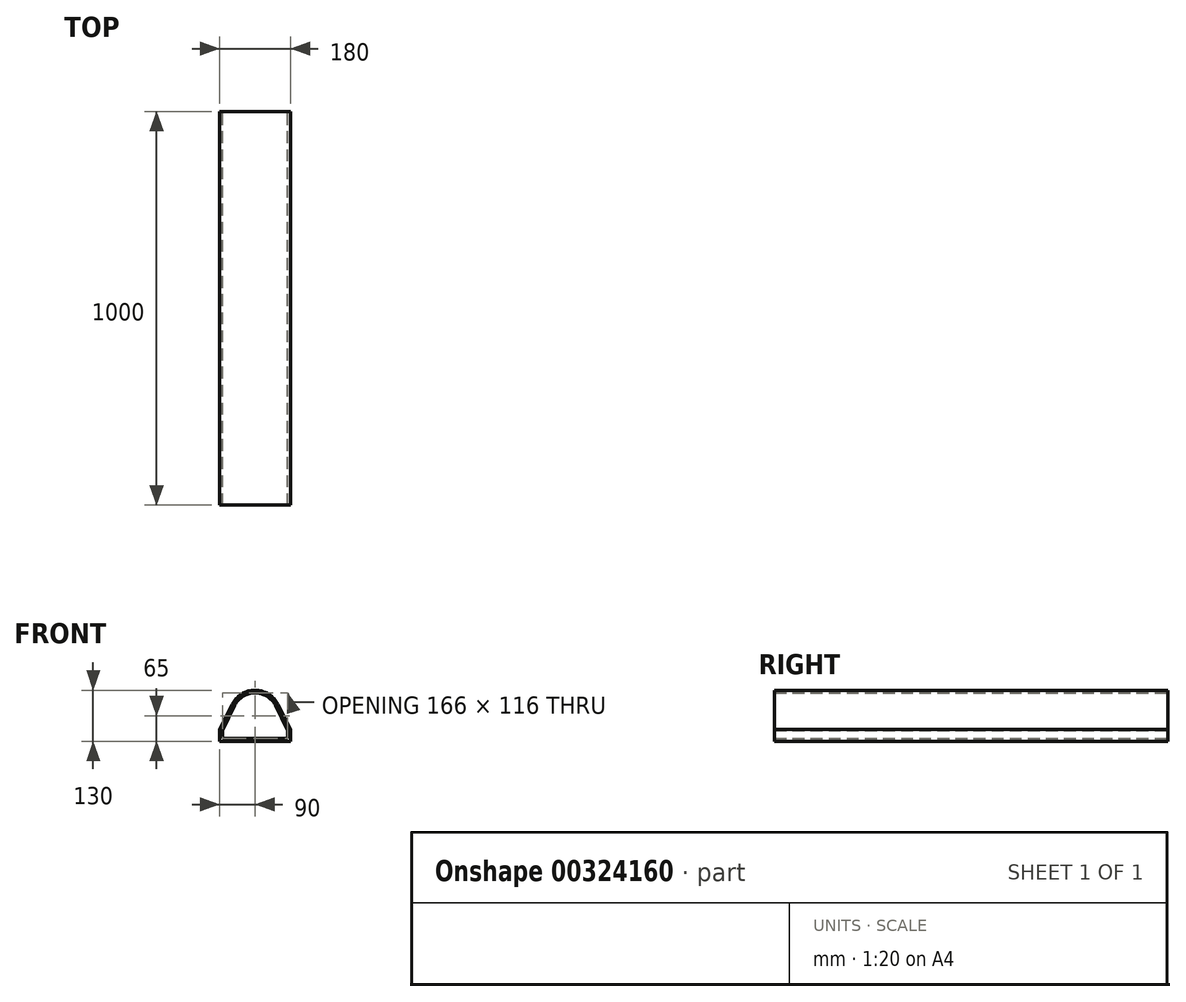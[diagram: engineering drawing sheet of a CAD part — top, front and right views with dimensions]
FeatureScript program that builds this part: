
annotation { "Feature Type Name" : "Feature", "Feature Type Description" : "" }
export const myFeature = defineFeature(function(context is Context, id is Id, definition is map)
    precondition{}
    {
        {
            var Q0;
            Q0=qCreatedBy(makeId("Front.planeOp"),FACE);
            var sketch = newSketch(context, id + "F0", { "sketchPlane" : qUnion([Q0])});
            skLineSegment(sketch, "E0", {"start": v(0, -65) * mm, "end": v(90, -65) * mm});
            skLineSegment(sketch, "E1", {"start": v(90, -65) * mm, "end": v(90, -35) * mm});
            skArc(sketch, "E2", {"start": v(58.2, 28.94) * mm, "mid": v(34.23, 55.26) * mm, "end": v(0, 65) * mm});
            skLineSegment(sketch, "E3", {"start": v(90, -35) * mm, "end": v(58.2, 28.94) * mm});
            skLineSegment(sketch, "E4", {"start": v(0, 67.77) * mm, "end": v(0, -93.23) * mm, "construction": true});
            skArc(sketch, "E5.0", {"start": v(51.93, 25.83) * mm, "mid": v(30.55, 49.3) * mm, "end": v(0, 58) * mm});
            skLineSegment(sketch, "E5.1", {"start": v(83, -36.64) * mm, "end": v(51.93, 25.83) * mm});
            skLineSegment(sketch, "E5.2", {"start": v(83, -58) * mm, "end": v(83, -36.64) * mm});
            skLineSegment(sketch, "E5.3", {"start": v(0, -58) * mm, "end": v(83, -58) * mm});
            skLineSegment(sketch, "E6.MirrorCS", {"start": v(0, -65) * mm, "end": v(-90, -65) * mm});
            skLineSegment(sketch, "E7.MirrorCS", {"start": v(-90, -65) * mm, "end": v(-90, -35) * mm});
            skArc(sketch, "E8.MirrorCS", {"start": v(-58.2, 28.94) * mm, "mid": v(-34.23, 55.26) * mm, "end": v(0, 65) * mm});
            skLineSegment(sketch, "E9.MirrorCS", {"start": v(-90, -35) * mm, "end": v(-58.2, 28.94) * mm});
            skLineSegment(sketch, "E10.MirrorCS", {"start": v(0, -58) * mm, "end": v(-83, -58) * mm});
            skArc(sketch, "E11.MirrorCS", {"start": v(-51.93, 25.83) * mm, "mid": v(-30.55, 49.3) * mm, "end": v(0, 58) * mm});
            skLineSegment(sketch, "E12.MirrorCS", {"start": v(-83, -58) * mm, "end": v(-83, -36.64) * mm});
            skLineSegment(sketch, "E13.MirrorCS", {"start": v(-83, -36.64) * mm, "end": v(-51.93, 25.83) * mm});
            skSolve(sketch);
        }
        {
            var Q0;
            Q0=makeQuery(id+"F0.imprint","IMPRINT",FACE,{"disambiguationData":[TD([[makeQuery(id+"F0.imprint","IMPRINT",EDGE,{"derivedFrom":sQuery(id+"F0.wireOp",EDGE,"E0")}),1.0]])]});
            extrude(context, id + "F1", {"entities" : qUnion([Q0]), "depth" : 1000 * mm});
        }
    });
